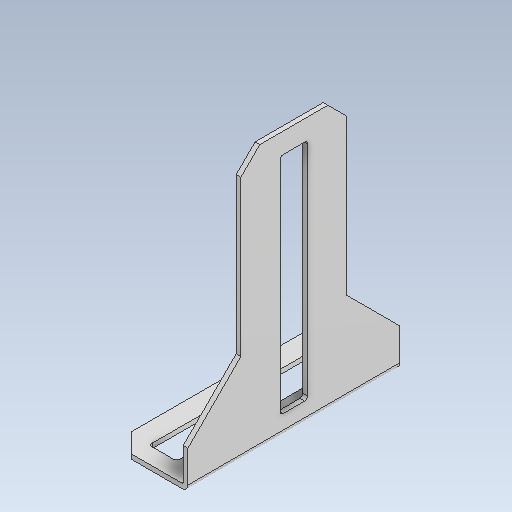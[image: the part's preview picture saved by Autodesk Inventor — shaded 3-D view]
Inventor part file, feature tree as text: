
AUTODESK INVENTOR PART (.ipt)
format: ipt  version: 2021 (Build 250183000, 183)  size: 127,488 bytes
history: mixed  units: in
note: dims shown in document units (in); Inventor stores cm internally (conversion verified against a paired STEP export)
features: fillet x1, imported_body x1
ambient origin geometry x8: Origin, YZ Plane, XZ Plane, XY Plane, X Axis, Y Axis, Z Axis, Center Point
bodies: Solid1 (imported_parasolid)
feature tree (2):
  fillet  "Fillet3"  [1 undecoded]
  imported_body  NMx_Import_Brep_tag  [imported B-rep: ~34 faces, bbox_mm=[12.7, 44.45, 35.56]]
note: 1 required parameter value undecoded (feature->parameter linkage not recoverable at this tier; creation-order binding heuristic only, values carry confidence <= 0.55)
